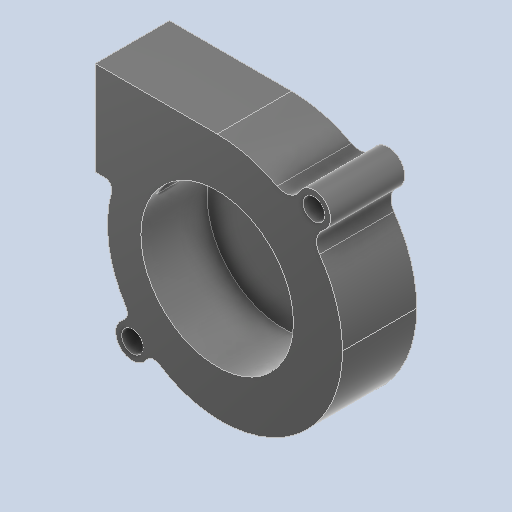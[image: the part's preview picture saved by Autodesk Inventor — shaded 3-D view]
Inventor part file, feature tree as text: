
AUTODESK INVENTOR PART (.ipt)
format: ipt  version: 2022 (Build 260153070, 153G)  size: 211,968 bytes
history: native  units: mm
features: extrude x3, sketch x3
ambient origin geometry x8: Origin, YZ Plane, XZ Plane, XY Plane, X Axis, Y Axis, Z Axis, Center Point
bodies: Solid1 (feature_tree)
feature tree (6):
  extrude  "Extrusion1"  Depth=19.7mm
  extrude  "Extrusion2"  Depth=17.8mm
  extrude  "Extrusion3"  Depth=13.9mm
  sketch  "Sketch1"  dims[d1=25.6mm d2=19.7mm]
  sketch  "Sketch2"  dims[d6=4.5mm d8=17.8mm]
  sketch  "Sketch3"  dims[d9=26.3mm d10=51.8mm d11=20.3mm d12=1.5mm d13=4.5mm d14=22.8mm d15=20.3mm d16=2.0mm d18=90.0deg d19=90.0deg d20=1.25mm d21=1.25mm d22=90.0deg d23=90.0deg d24=15.6mm d25=0.0mm d26=12.6mm d27=17.1mm d28=1.7mm d29=1.45mm d30=15.6mm d31=0.0mm d32=32.0mm d33=13.9mm d34=0.0mm]
